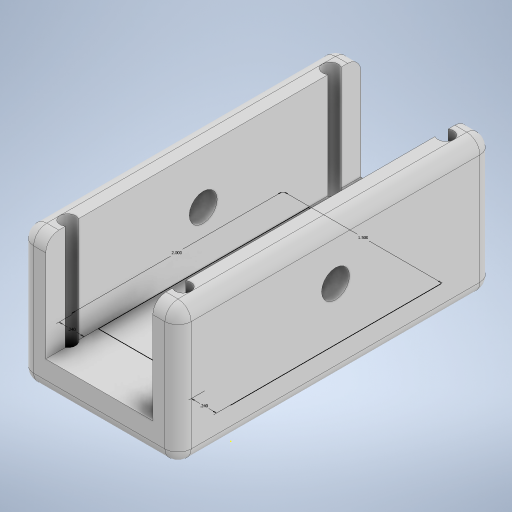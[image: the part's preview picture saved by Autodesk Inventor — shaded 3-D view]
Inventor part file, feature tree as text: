
AUTODESK INVENTOR PART (.ipt)
format: ipt  version: 2024.1 (Build 281209000, 209)  size: 348,160 bytes
history: native  units: in
note: dims shown in document units (in); Inventor stores cm internally (conversion verified against a paired STEP export)
features: extrude x5, sketch x5, hole x2, projected_geometry x2, fillet x1
ambient origin geometry x8: Origin, YZ Plane, XZ Plane, XY Plane, X Axis, Y Axis, Z Axis, Center Point
bodies: Solid1 (feature_tree)
feature tree (15):
  extrude  "Extrusion1"  Depth=2.0in
  extrude  "Extrusion2"  Depth=0.24in
  hole  "Hole1"  [1 undecoded]
  extrude  "Extrusion3"  Depth=0.125in TaperAngle=0.0deg
  extrude  "Extrusion4"  Depth=0.125in TaperAngle=0.0deg
  extrude  "Extrusion5"  Depth=0.6in
  sketch  "Sketch6"  dims[d8=0.5in]
  hole  "Hole2"  [1 undecoded]
  fillet  "Fillet1"  Radius=0.5in
  sketch  "Sketch3"  dims[d0=1.5in d1=2.0in]
  projected_geometry  "Projected Loop1"
  sketch  "Sketch4"  dims[d2=0.24in d3=0.24in]
  projected_geometry  "Projected Loop2"
  sketch  "Sketch5"  dims[d4=1.0in d5=0.0in d6=0.2in d7=0.0in]
  sketch  "Sketch7"  dims[d9=0.266in d10=0.75in d11=0.438in d12=0.25in d13=0.5635in d14=1.0in d15=0.8108in d16=0.5in d17=0.0in d18=0.5in d19=0.0in d20=0.6in d21=2.0in d22=0.5in d23=1.75in d24=0.5in d25=0.1in d26=0.0in d27=0.2in d28=0.25in d29=0.2in d30=0.25in d31=0.2in d32=0.25in d33=0.2in d34=0.1495in d35=0.75in d36=0.375in d37=0.25in d38=0.5635in d39=1.0in d40=0.8108in d41=0.125in]
note: 2 required parameter values undecoded (feature->parameter linkage not recoverable at this tier; creation-order binding heuristic only, values carry confidence <= 0.55)
